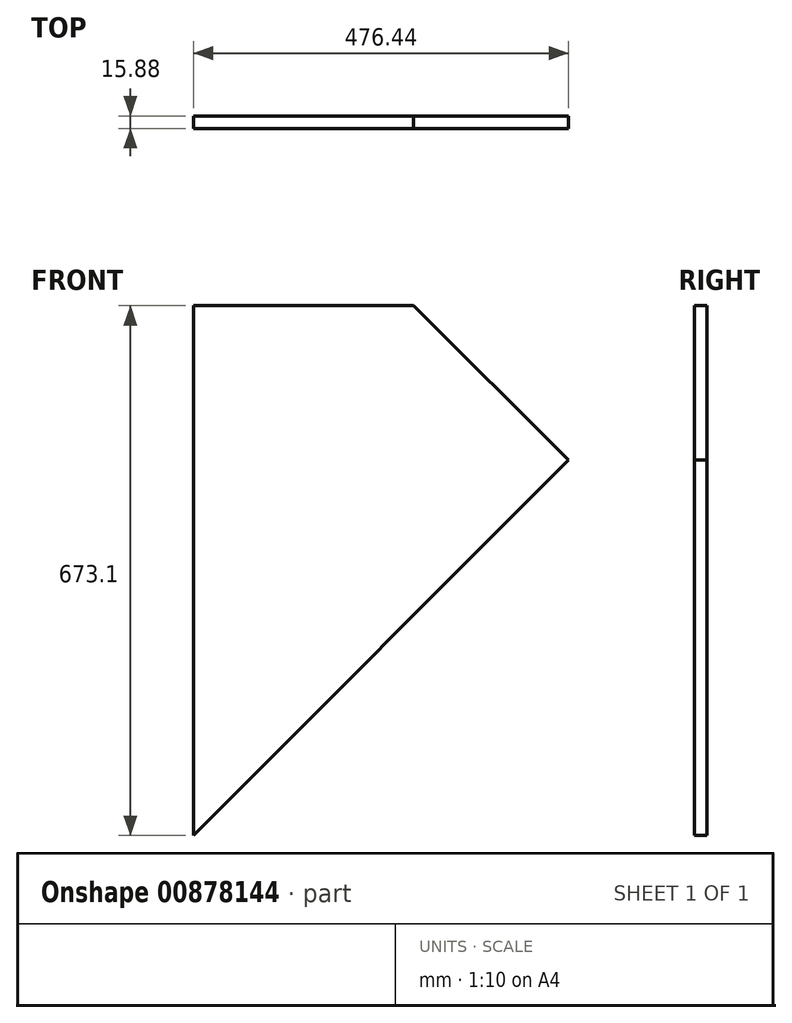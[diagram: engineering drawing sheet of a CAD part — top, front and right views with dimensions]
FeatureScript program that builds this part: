
annotation { "Feature Type Name" : "Feature", "Feature Type Description" : "" }
export const myFeature = defineFeature(function(context is Context, id is Id, definition is map)
    precondition{}
    {
        {
            var Q0;
            Q0=qCreatedBy(makeId("Front.planeOp"),FACE);
            var sketch = newSketch(context, id + "F0", { "sketchPlane" : qUnion([Q0])});
            skLineSegment(sketch, "E0", {"start": v(0, 0) * mm, "end": v(0, 673.1) * mm});
            skLineSegment(sketch, "E1", {"start": v(0, 673.1) * mm, "end": v(279.4, 673.1) * mm});
            skLineSegment(sketch, "E2", {"start": v(279.4, 673.1) * mm, "end": v(476.44, 476.99) * mm});
            skLineSegment(sketch, "E3", {"start": v(476.44, 476.99) * mm, "end": v(0, 0) * mm});
            skSolve(sketch);
        }
        {
            var Q0;
            Q0 = qSketchRegion(id + "F0", true);
            extrude(context, id + "F1", {"entities" : qUnion([Q0]), "depth" : 15.88 * mm, "offsetDistance" : 25.4 * mm});
        }
    });
